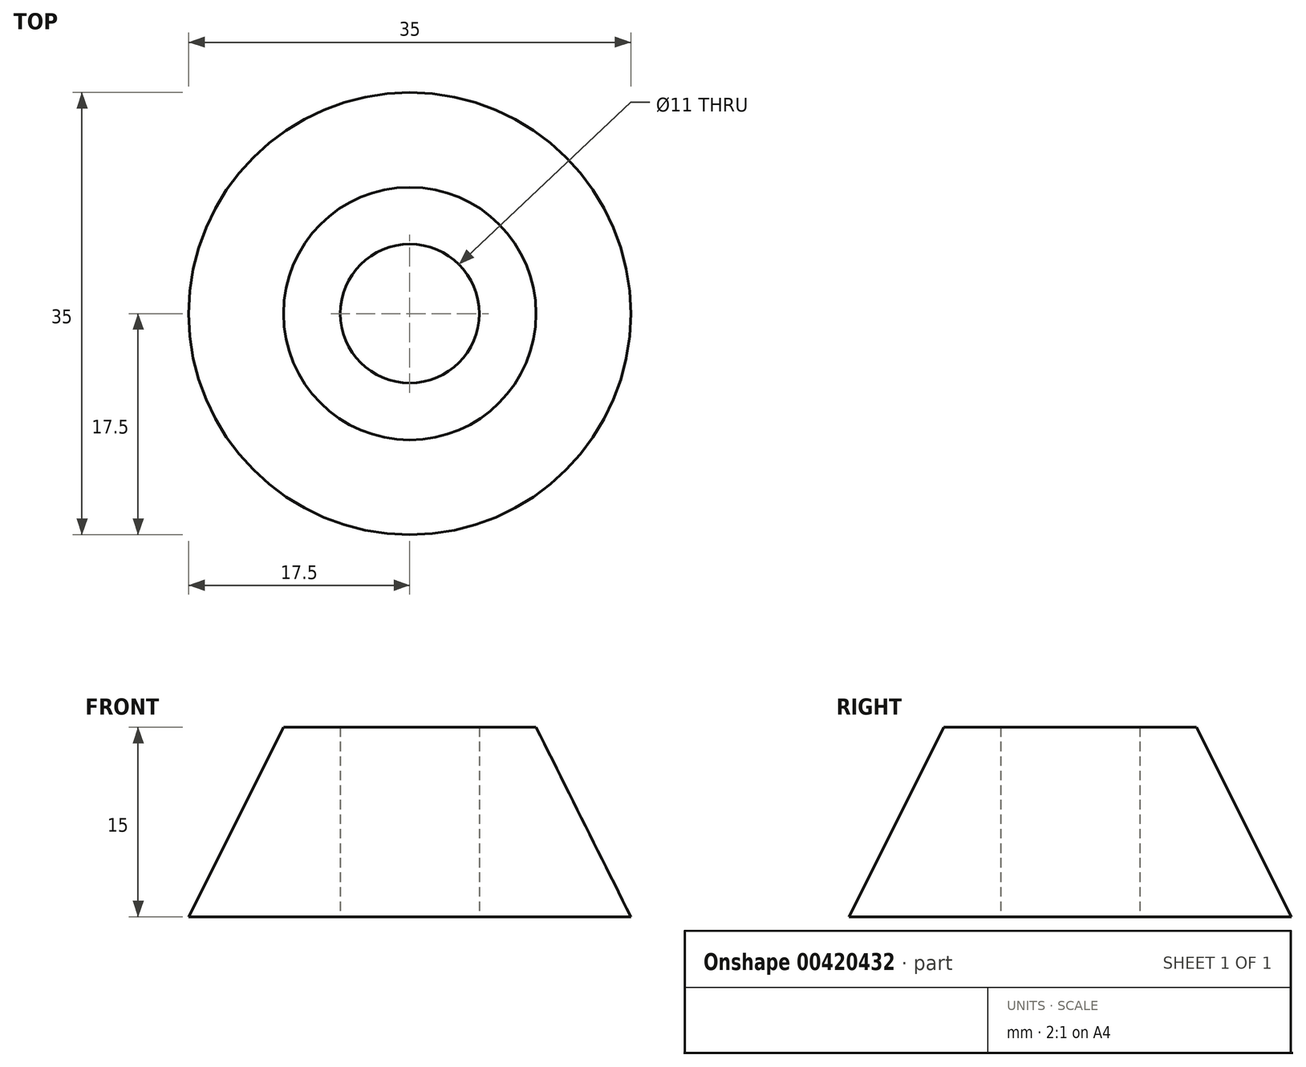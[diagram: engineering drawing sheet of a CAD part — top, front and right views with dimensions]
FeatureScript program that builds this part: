
annotation { "Feature Type Name" : "Feature", "Feature Type Description" : "" }
export const myFeature = defineFeature(function(context is Context, id is Id, definition is map)
    precondition{}
    {
        {
            var Q0;
            Q0=qCreatedBy(makeId("Top.planeOp"),FACE);
            var sketch = newSketch(context, id + "F0", { "sketchPlane" : qUnion([Q0])});
            skCircle(sketch, "E0", {"center": v(0, 0) * mm, "radius": 5.5 * mm});
            skCircle(sketch, "E1", {"center": v(0, 0) * mm, "radius": 10 * mm});
            skCircle(sketch, "E2", {"center": v(0, 0) * mm, "radius": 17.5 * mm});
            skSolve(sketch);
        }
        {
            var Q0;
            Q0 = qSketchRegion(id + "F0", true);
            var Q1;
            Q1=makeQuery(id+"F0.imprint","IMPRINT",FACE,{"disambiguationData":[TD([[makeQuery(id+"F0.imprint","IMPRINT",EDGE,{"derivedFrom":sQuery(id+"F0.wireOp",EDGE,"E0")}),-1.0]])]});
            extrude(context, id + "F1", {"entities" : qUnion([Q0, Q1]), "depth" : 15 * mm, "offsetDistance" : 25 * mm});
        }
        {
            var Q0;
            Q0=makeQuery(id+"F1.opExtrude","CAP_EDGE",EDGE,{"disambiguationData":[OSD([sQuery(id+"F0.wireOp",EDGE,"E2")])],"isStart":false});
            chamfer(context, id + "F2", {"entities" : qUnion([Q0]), "chamferType" : ChamferType.TWO_OFFSETS, "width1" : 7.5 * mm, "oppositeDirection" : false, "width2" : 15 * mm, "tangentPropagation" : true});
        }
    });
